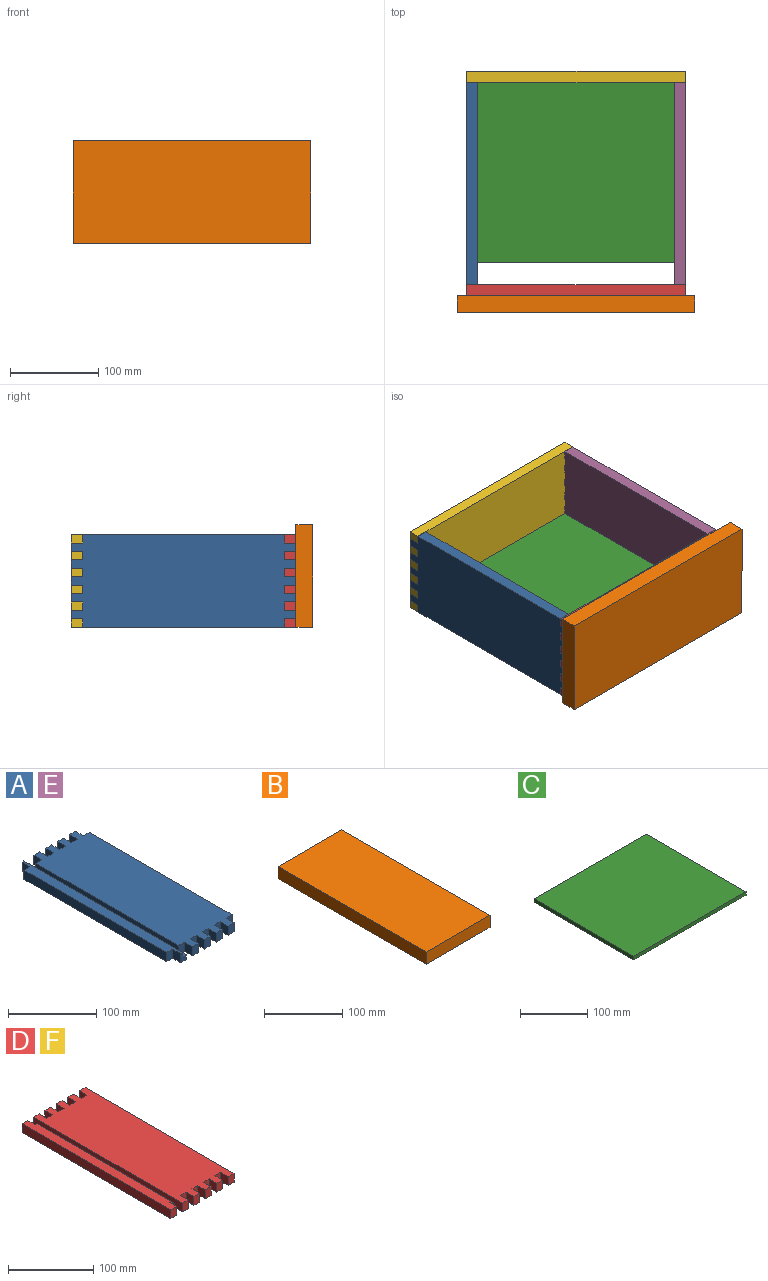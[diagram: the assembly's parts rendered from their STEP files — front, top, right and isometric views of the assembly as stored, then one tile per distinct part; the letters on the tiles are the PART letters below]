
ASSEMBLY  parts=6 mates=5
PART A: 50 faces, bbox 104.8x254x12.7 mm
  f0: plane 254x85.73mm, normal (0,0,1), area 20564.5mm2, adj f5,f7,f8,f9,f10,f11,f12,f13
  f1: plane 12.7x9.53mm, normal (0,1,0), area 80.6mm2, adj f3,f4,f6,f20,f48,f49
  f2: plane 12.7x6.35mm, normal (1,0,0), area 80.6mm2, adj f6,f16,f21,f49
  f3: plane 12.7x6.35mm, normal (1,0,0), area 80.6mm2, adj f1,f6,f23,f49
  f4: plane 254x12.7mm, normal (0,0,1), area 2983.9mm2, adj f1,f15,f16,f17,f18,f19,f20,f48
  f5: plane 228.6x12.7mm, normal (1,0,0), area 2903.2mm2, adj f0,f6,f43,f46
  f6: plane 254x104.78mm, normal (0,0,-1), area 25161.2mm2, adj f1,f2,f3,f5,f7,f8,f9,f10
  f7: plane 12.7x9.53mm, normal (0,-1,0), area 121mm2, adj f0,f6,f39,f44
  f8: plane 12.7x9.53mm, normal (0,1,0), area 121mm2, adj f0,f6,f42,f45
  f9: plane 12.7x9.53mm, normal (0,-1,0), area 121mm2, adj f0,f6,f33,f38
  f10: plane 12.7x9.53mm, normal (0,1,0), area 121mm2, adj f0,f6,f36,f40
  f11: plane 12.7x9.53mm, normal (0,-1,0), area 121mm2, adj f0,f6,f27,f32
  f12: plane 12.7x9.53mm, normal (0,1,0), area 121mm2, adj f0,f6,f30,f34
  f13: plane 12.7x9.53mm, normal (0,-1,0), area 121mm2, adj f0,f6,f22,f26
  f14: plane 12.7x9.53mm, normal (0,1,0), area 121mm2, adj f0,f6,f24,f28
  f15: plane 228.6x12.7mm, normal (-1,0,0), area 2903.2mm2, adj f4,f6,f17,f19
  f16: plane 12.7x9.53mm, normal (0,-1,0), area 80.6mm2, adj f2,f4,f6,f18,f48,f49
  f17: plane 12.7x9.53mm, normal (0,-1,0), area 121mm2, adj f4,f6,f15,f18
  f18: plane 12.7x12.7mm, normal (-1,0,0), area 161.3mm2, adj f4,f6,f16,f17
  f19: plane 12.7x9.53mm, normal (0,1,0), area 121mm2, adj f4,f6,f15,f20
  f20: plane 12.7x12.7mm, normal (-1,0,0), area 161.3mm2, adj f1,f4,f6,f19
  f21: plane 12.7x9.53mm, normal (0,-1,0), area 121mm2, adj f0,f2,f6,f22,f47
  f22: plane 12.7x12.7mm, normal (-1,0,0), area 161.3mm2, adj f0,f6,f13,f21
  f23: plane 12.7x9.53mm, normal (0,1,0), area 121mm2, adj f0,f3,f6,f24,f47
  f24: plane 12.7x12.7mm, normal (-1,0,0), area 161.3mm2, adj f0,f6,f14,f23
  f25: plane 12.7x9.53mm, normal (0,-1,0), area 121mm2, adj f0,f6,f26,f27
  f26: plane 12.7x12.7mm, normal (1,0,0), area 161.3mm2, adj f0,f6,f13,f25
  f27: plane 12.7x12.7mm, normal (-1,0,0), area 161.3mm2, adj f0,f6,f11,f25
  f28: plane 12.7x12.7mm, normal (1,0,0), area 161.3mm2, adj f0,f6,f14,f29
  f29: plane 12.7x9.53mm, normal (0,1,0), area 121mm2, adj f0,f6,f28,f30
  f30: plane 12.7x12.7mm, normal (-1,0,0), area 161.3mm2, adj f0,f6,f12,f29
  f31: plane 12.7x9.53mm, normal (0,-1,0), area 121mm2, adj f0,f6,f32,f33
  f32: plane 12.7x12.7mm, normal (1,0,0), area 161.3mm2, adj f0,f6,f11,f31
  f33: plane 12.7x12.7mm, normal (-1,0,0), area 161.3mm2, adj f0,f6,f9,f31
  f34: plane 12.7x12.7mm, normal (1,0,0), area 161.3mm2, adj f0,f6,f12,f35
  f35: plane 12.7x9.53mm, normal (0,1,0), area 121mm2, adj f0,f6,f34,f36
  f36: plane 12.7x12.7mm, normal (-1,0,0), area 161.3mm2, adj f0,f6,f10,f35
  f37: plane 12.7x9.53mm, normal (0,-1,0), area 121mm2, adj f0,f6,f38,f39
  f38: plane 12.7x12.7mm, normal (1,0,0), area 161.3mm2, adj f0,f6,f9,f37
  f39: plane 12.7x12.7mm, normal (-1,0,0), area 161.3mm2, adj f0,f6,f7,f37
  f40: plane 12.7x12.7mm, normal (1,0,0), area 161.3mm2, adj f0,f6,f10,f41
  f41: plane 12.7x9.53mm, normal (0,1,0), area 121mm2, adj f0,f6,f40,f42
  f42: plane 12.7x12.7mm, normal (-1,0,0), area 161.3mm2, adj f0,f6,f8,f41
  f43: plane 12.7x9.53mm, normal (0,-1,0), area 121mm2, adj f0,f5,f6,f44
  f44: plane 12.7x12.7mm, normal (1,0,0), area 161.3mm2, adj f0,f6,f7,f43
  f45: plane 12.7x12.7mm, normal (1,0,0), area 161.3mm2, adj f0,f6,f8,f46
  f46: plane 12.7x9.53mm, normal (0,1,0), area 121mm2, adj f0,f5,f6,f45
  f47: plane 228.6x6.35mm, normal (-1,0,0), area 1451.6mm2, adj f0,f21,f23,f49
  f48: plane 254x6.35mm, normal (1,0,0), area 1612.9mm2, adj f1,f4,f16,f49
  f49: plane 254x6.35mm, normal (0,0,1), area 1612.9mm2, adj f1,f2,f3,f16,f47,f48
PART B: 6 faces, bbox 115.9x268.3x19.1 mm
  f0: plane 268.29x19.05mm, normal (-1,0,0), area 5110.9mm2, adj f1,f3,f4,f5
  f1: plane 115.89x19.05mm, normal (0,-1,0), area 2207.7mm2, adj f0,f2,f4,f5
  f2: plane 268.29x19.05mm, normal (1,0,0), area 5110.9mm2, adj f1,f3,f4,f5
  f3: plane 115.89x19.05mm, normal (0,1,0), area 2207.7mm2, adj f0,f2,f4,f5
  f4: plane 268.29x115.89mm, normal (0,0,1), area 31091.2mm2, adj f0,f1,f2,f3
  f5: plane 268.29x115.89mm, normal (0,0,-1), area 31091.2mm2, adj f0,f1,f2,f3
PART C: 6 faces, bbox 235x209.6x6.4 mm
  f0: plane 209.55x6.35mm, normal (-1,0,0), area 1330.6mm2, adj f1,f3,f4,f5
  f1: plane 234.95x6.35mm, normal (0,-1,0), area 1491.9mm2, adj f0,f2,f4,f5
  f2: plane 209.55x6.35mm, normal (1,0,0), area 1330.6mm2, adj f1,f3,f4,f5
  f3: plane 234.95x6.35mm, normal (0,1,0), area 1491.9mm2, adj f0,f2,f4,f5
  f4: plane 234.95x209.55mm, normal (0,0,1), area 49233.8mm2, adj f0,f1,f2,f3
  f5: plane 234.95x209.55mm, normal (0,0,-1), area 49233.8mm2, adj f0,f1,f2,f3
PART D: 48 faces, bbox 104.8x247.7x12.7 mm
  f0: plane 247.65x85.73mm, normal (0,0,1), area 20262.1mm2, adj f2,f3,f6,f7,f8,f9,f10,f11
  f1: plane 12.7x9.53mm, normal (0,-1,0), area 80.6mm2, adj f4,f5,f18,f21,f46,f47
  f2: plane 12.7x9.53mm, normal (0,-1,0), area 121mm2, adj f0,f5,f16,f41
  f3: plane 12.7x9.53mm, normal (0,1,0), area 121mm2, adj f0,f5,f16,f45
  f4: plane 247.65x12.7mm, normal (0,0,1), area 3064.5mm2, adj f1,f14,f15,f17,f18,f19,f20,f46
  f5: plane 247.65x104.78mm, normal (0,0,-1), area 24737.9mm2, adj f1,f2,f3,f6,f7,f8,f9,f10
  f6: plane 12.7x9.53mm, normal (0,-1,0), area 121mm2, adj f0,f5,f35,f40
  f7: plane 12.7x9.53mm, normal (0,1,0), area 121mm2, adj f0,f5,f39,f43
  f8: plane 12.7x9.53mm, normal (0,-1,0), area 121mm2, adj f0,f5,f29,f34
  f9: plane 12.7x9.53mm, normal (0,1,0), area 121mm2, adj f0,f5,f33,f37
  f10: plane 12.7x9.53mm, normal (0,-1,0), area 121mm2, adj f0,f5,f23,f28
  f11: plane 12.7x9.53mm, normal (0,1,0), area 121mm2, adj f0,f5,f27,f31
  f12: plane 12.7x9.53mm, normal (0,-1,0), area 121mm2, adj f0,f5,f21,f22
  f13: plane 12.7x9.53mm, normal (0,1,0), area 121mm2, adj f0,f5,f21,f25
  f14: plane 247.65x12.7mm, normal (-1,0,0), area 3145.2mm2, adj f4,f5,f15,f17
  f15: plane 12.7x9.53mm, normal (0,-1,0), area 121mm2, adj f4,f5,f14,f18
  f16: plane 247.65x12.7mm, normal (1,0,0), area 3145.2mm2, adj f0,f2,f3,f5
  f17: plane 12.7x9.53mm, normal (0,1,0), area 121mm2, adj f4,f5,f14,f19
  f18: plane 12.7x12.7mm, normal (1,0,0), area 161.3mm2, adj f1,f4,f5,f15
  f19: plane 12.7x12.7mm, normal (1,0,0), area 161.3mm2, adj f4,f5,f17,f20
  f20: plane 12.7x9.53mm, normal (0,1,0), area 80.6mm2, adj f4,f5,f19,f21,f46,f47
  f21: plane 247.65x12.7mm, normal (-1,0,0), area 1733.9mm2, adj f0,f1,f5,f12,f13,f20,f47
  f22: plane 12.7x12.7mm, normal (1,0,0), area 161.3mm2, adj f0,f5,f12,f24
  f23: plane 12.7x12.7mm, normal (-1,0,0), area 161.3mm2, adj f0,f5,f10,f24
  f24: plane 12.7x9.53mm, normal (0,-1,0), area 121mm2, adj f0,f5,f22,f23
  f25: plane 12.7x12.7mm, normal (1,0,0), area 161.3mm2, adj f0,f5,f13,f26
  f26: plane 12.7x9.53mm, normal (0,1,0), area 121mm2, adj f0,f5,f25,f27
  f27: plane 12.7x12.7mm, normal (-1,0,0), area 161.3mm2, adj f0,f5,f11,f26
  f28: plane 12.7x12.7mm, normal (1,0,0), area 161.3mm2, adj f0,f5,f10,f30
  f29: plane 12.7x12.7mm, normal (-1,0,0), area 161.3mm2, adj f0,f5,f8,f30
  f30: plane 12.7x9.53mm, normal (0,-1,0), area 121mm2, adj f0,f5,f28,f29
  f31: plane 12.7x12.7mm, normal (1,0,0), area 161.3mm2, adj f0,f5,f11,f32
  f32: plane 12.7x9.53mm, normal (0,1,0), area 121mm2, adj f0,f5,f31,f33
  f33: plane 12.7x12.7mm, normal (-1,0,0), area 161.3mm2, adj f0,f5,f9,f32
  f34: plane 12.7x12.7mm, normal (1,0,0), area 161.3mm2, adj f0,f5,f8,f36
  f35: plane 12.7x12.7mm, normal (-1,0,0), area 161.3mm2, adj f0,f5,f6,f36
  f36: plane 12.7x9.53mm, normal (0,-1,0), area 121mm2, adj f0,f5,f34,f35
  f37: plane 12.7x12.7mm, normal (1,0,0), area 161.3mm2, adj f0,f5,f9,f38
  f38: plane 12.7x9.53mm, normal (0,1,0), area 121mm2, adj f0,f5,f37,f39
  f39: plane 12.7x12.7mm, normal (-1,0,0), area 161.3mm2, adj f0,f5,f7,f38
  f40: plane 12.7x12.7mm, normal (1,0,0), area 161.3mm2, adj f0,f5,f6,f42
  f41: plane 12.7x12.7mm, normal (-1,0,0), area 161.3mm2, adj f0,f2,f5,f42
  f42: plane 12.7x9.53mm, normal (0,-1,0), area 121mm2, adj f0,f5,f40,f41
  f43: plane 12.7x12.7mm, normal (1,0,0), area 161.3mm2, adj f0,f5,f7,f44
  f44: plane 12.7x9.53mm, normal (0,1,0), area 121mm2, adj f0,f5,f43,f45
  f45: plane 12.7x12.7mm, normal (-1,0,0), area 161.3mm2, adj f0,f3,f5,f44
  f46: plane 222.25x6.35mm, normal (1,0,0), area 1411.3mm2, adj f1,f4,f20,f47
  f47: plane 222.25x6.35mm, normal (0,0,1), area 1411.3mm2, adj f1,f20,f21,f46
PART E: same geometry as A
PART F: same geometry as D
PLACE A rot(axis=(0.71,0,0.71),180deg) t=(-114.3,254,-194.44)mm
PLACE B rot(axis=(0.58,-0.58,0.58),120deg) t=(143.67,0,-377.66)mm
PLACE C rot(axis=(0.02,0,1),0deg) t=(-650.01,38.1,12.7)mm
PLACE D rot(axis=(-0.58,-0.58,-0.58),120deg) t=(-114.3,0,0)mm
PLACE E rot(axis=(0,-1,0),90deg) t=(133.35,0,-194.44)mm
PLACE F rot(axis=(0.58,-0.58,0.58),120deg) t=(133.35,254,0)mm
MATE fastened B.f5 <-> D.f5  axis (0,1,0) through (9.52,0,0)mm
MATE fastened C.f4 <-> F.f21  axis (0,0,1) through (9.52,247.65,19.05)mm
MATE fastened F.f45 <-> A.f44  axis (0,0,-1) through (-107.95,247.65,95.25)mm
MATE fastened E.f44 <-> D.f45  axis (0,0,1) through (133.35,0,95.25)mm
MATE fastened A.f45 <-> D.f41  axis (0,0,1) through (-114.3,0,95.25)mm
